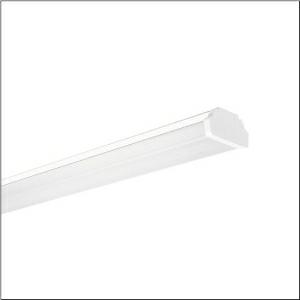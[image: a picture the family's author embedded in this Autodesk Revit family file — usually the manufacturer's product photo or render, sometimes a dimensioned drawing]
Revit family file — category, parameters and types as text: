
# Revit family: dus_r__31_gen_2_53bd813dv4dxd2_23c6
name_source: partatom
category: Lighting Fixtures
units: mm (PartAtom-declared; Revit-internal decimal feet)

## family parameters
Cut with Voids When Loaded = No
Host = Face
Light Source = No
Part Type = Normal
Room Calculation Point = No
Round Connector Dimension = Use Diameter
Shared = No

## types (1)
- --- (1 x LED, 13370 lm, 74.9 W, 4000K)
    Apparent Load = 75 VA
    CIE Flux Codes = 62 83 95 93 100
    Color Rendering = 80
    Color Temperature = 4000K
    Default Elevation = 1800 mm
    Description = DUS® 31 Gen.2, luminaire insert, of sheet steel, coil coated, white, length: 1.535mm, width: 81mm, height: 90mm, 5x system unit, system units: 307mm, LED rated luminous flux: 13.370lm, light colour: 840, control gear: DALI 2, control gear: ECG DALI, with plug, 5-pole, with phase selection, mains connection: 220..240V, AC, 50/60Hz, rated input power: 75W, through-wiring accessed according to module size, primary optical cover: cover, of PMMA, light emission: direct distribution, primary light characteristic: symmetric, protection rating (complete): IP20, protection rating (LED compartment): IP50, insulation class (complete): insulation class I (protective earthing), certification: CE, ENEC, VDE, UKCA, impact resistance: IK03, permissible ambient temperature for indoor applications: -25..+35°C, corresponds to IFS (International Featured Standards) requirements for safety and quality in the food industry, reducing of maximum allowable ambient temperature of 5°C with ceiling mounting, packaging unit: 1 piece
    Height = 95 mm
    Lamp = 1 x LED
    Lamp Light Flux = 13370 lm
    Lamp Power = 74.9 W
    Lamp count = 1
    Length = 1535 mm
    Luminous efficacy = 179 lm/W
    Manufacturer = Siteco
    ModVariant = No
    Model = 53BD813DV4DXD2
    Mounting Place = Ceiling
    Mounting Type = Pendant
    Number of Poles = 1
    OnlyDefault = Yes
    Power Factor = 1
    Product Name = DUS® 31 Gen.2
    Product group = luminaire insert | ceiling pendant
    ProductGroupID = 902
    Protection Class = Protection class I
    Protection Degree = IP 20
    RLX_Detail_Level = 1
    RLX_Emergency_Light_Flux = 0 lm
    RLX_Emergency_Type = 0
    RLX_Emergency_Type_DB = No
    RlxData = <blob elided: 32293 chars, md5=de156f60>
    Socket = socket
    Standby Power = 0 W
    System Light Flux = 13370 lm
    System Power = 75 W
    Type Comments = factory setting: luminous flux: 100 % | dim-lin: 254 | 511 mA
    Type Image = l_1319596.jpg
    URL = http://relux.com
    VarID = @adj_063747
    Voltage = 0 V
    Weight = 0.00 kg
    Width = 81 mm

## geometry (parser evidence)
native form markers: Blend x4, Sweep x13
no freeform markers — native parametric forms only
